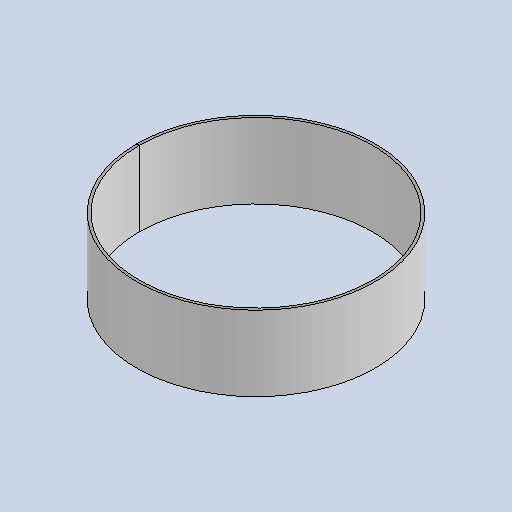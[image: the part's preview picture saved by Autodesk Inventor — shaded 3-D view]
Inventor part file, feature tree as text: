
AUTODESK INVENTOR PART (.ipt)
format: ipt  version: 2025.1 (Build 291241020, 241B)  size: 135,168 bytes
history: native  units: mm
features: sketch x2, revolve x1, extrude x1, other x1
ambient origin geometry x8: Origin, YZ Plane, XZ Plane, XY Plane, X Axis, Y Axis, Z Axis, Center Point
bodies: Solid1 (feature_tree)
feature tree (5):
  revolve  "Revolution1"  [1 undecoded]
  extrude  "Extrusion1"  Depth=62.8144mm
  sketch  "Sketch1"  dims[d1=6.0mm d3=6.0mm d4=530.0mm]
  sketch  "Sketch2"  dims[d5=120.0mm d6=62.8144mm d7=6.0mm d8=50.0mm d9=952.0mm d10=0.0mm d11=0.0mm]
  other  "Definition1"
note: 1 required parameter value undecoded (feature->parameter linkage not recoverable at this tier; creation-order binding heuristic only, values carry confidence <= 0.55)
